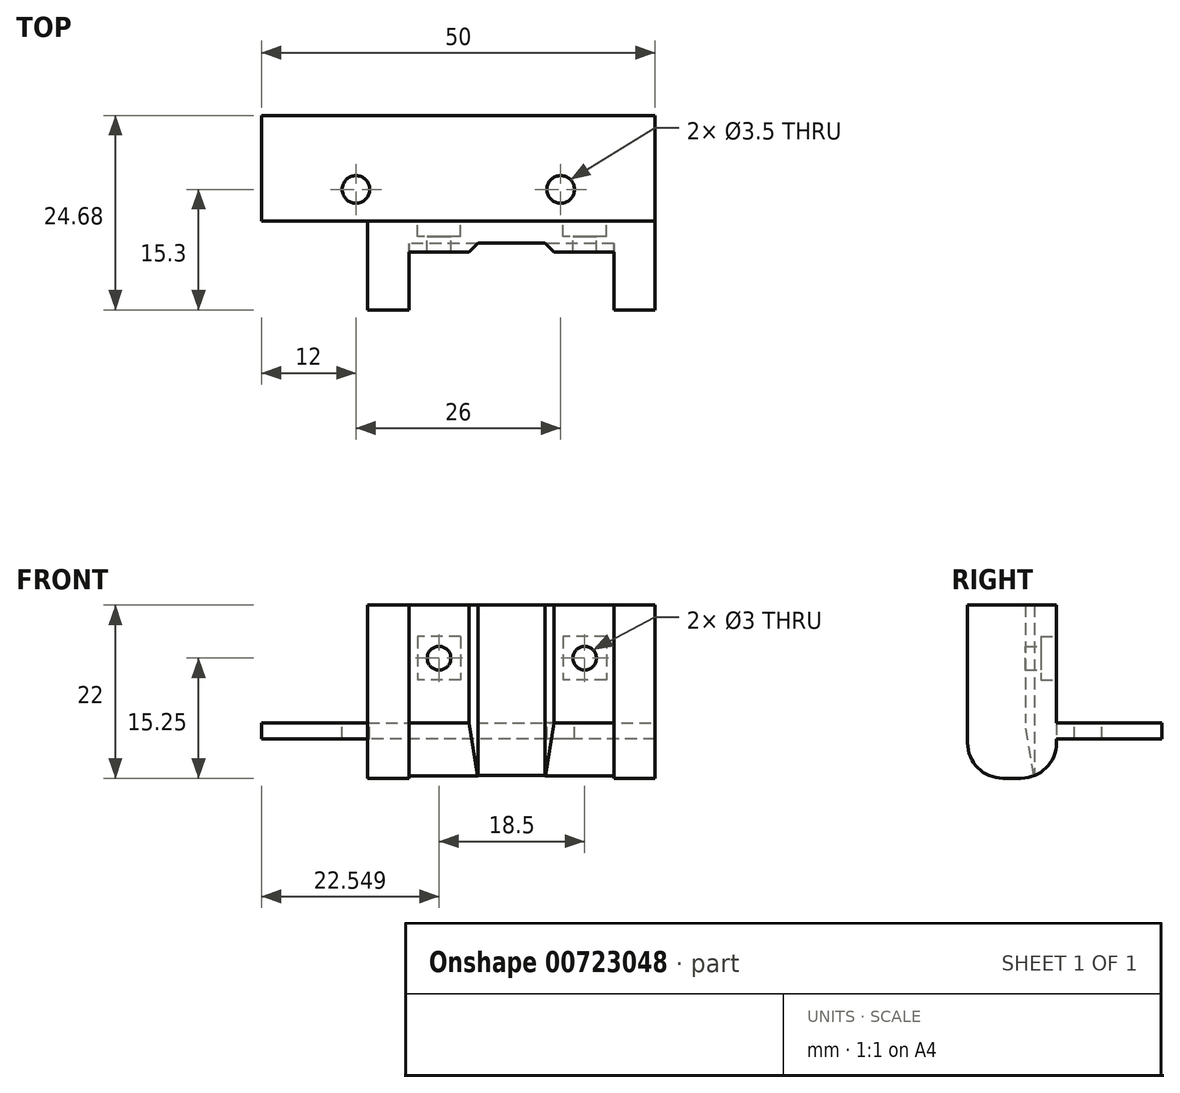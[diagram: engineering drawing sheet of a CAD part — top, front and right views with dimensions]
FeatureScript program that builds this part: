
annotation { "Feature Type Name" : "Feature", "Feature Type Description" : "" }
export const myFeature = defineFeature(function(context is Context, id is Id, definition is map)
    precondition{}
    {
        {
            var Q0;
            Q0=qCreatedBy(makeId("Right.planeOp"),FACE);
            var sketch = newSketch(context, id + "F0", { "sketchPlane" : qUnion([Q0])});
            skLineSegment(sketch, "E0", {"start": v(0, 0) * mm, "end": v(13.38, 0) * mm});
            skLineSegment(sketch, "E1", {"start": v(13.38, 0) * mm, "end": v(13.38, 2) * mm});
            skLineSegment(sketch, "E2", {"start": v(13.38, 2) * mm, "end": v(0, 2) * mm});
            skLineSegment(sketch, "E3", {"start": v(0, 2) * mm, "end": v(0, 0) * mm});
            skSolve(sketch);
        }
        {
            var Q0;
            Q0=makeQuery(id+"F0.imprint","IMPRINT",FACE,{"disambiguationData":[TD([[makeQuery(id+"F0.imprint","IMPRINT",EDGE,{"derivedFrom":sQuery(id+"F0.wireOp",EDGE,"E0")}),1.0]])]});
            extrude(context, id + "F1", {"entities" : qUnion([Q0]), "endBound" : BoundingType.SYMMETRIC, "depth" : 50 * mm});
        }
        {
            var Q0;
            Q0=makeQuery(id+"F1.opExtrude","SWEPT_FACE",FACE,{"disambiguationData":[OSD([sQuery(id+"F0.wireOp",EDGE,"E2")])]});
            var sketch = newSketch(context, id + "F2", { "sketchPlane" : qUnion([Q0])});
            skLineSegment(sketch, "E4", {"start": v(-25, 4) * mm, "end": v(25, 4) * mm, "construction": true});
            skLineSegment(sketch, "E5", {"start": v(0, 13.38) * mm, "end": v(0, 0) * mm, "construction": true});
            skCircle(sketch, "E6", {"center": v(-13, 4) * mm, "radius": 1.75 * mm});
            skCircle(sketch, "E7", {"center": v(13, 4) * mm, "radius": 1.75 * mm});
            skSolve(sketch);
        }
        {
            var Q0;
            Q0=qSketchRegion(id+"F2",true);
            extrude(context, id + "F3", {"entities" : qUnion([Q0]), "operationType" : NewBodyOperationType.REMOVE, "endBound" : BoundingType.UP_TO_NEXT, "oppositeDirection" : true, "depth" : 25 * mm});
        }
        {
            var Q0;
            Q0=qCreatedBy(makeId("Right.planeOp"),FACE);
            var sketch = newSketch(context, id + "F4", { "sketchPlane" : qUnion([Q0])});
            skLineSegment(sketch, "E8.bottom", {"start": v(0, 2) * mm, "end": v(-11.3, 2) * mm});
            skLineSegment(sketch, "E8.top", {"start": v(0, -5) * mm, "end": v(-11.3, -5) * mm});
            skLineSegment(sketch, "E8.left", {"start": v(0, 2) * mm, "end": v(0, -5) * mm});
            skLineSegment(sketch, "E8.right", {"start": v(-11.3, 2) * mm, "end": v(-11.3, -5) * mm});
            skSolve(sketch);
        }
        {
            var Q0;
            Q0=qSketchRegion(id+"F4",true);
            var Q1;
            Q1=makeQuery(id+"F1.opExtrude","CAP_FACE",FACE,{"disambiguationData":[OSD([sQuery(id+"F0.wireOp",EDGE,"E0"),sQuery(id+"F0.wireOp",EDGE,"E1"),sQuery(id+"F0.wireOp",EDGE,"E2"),sQuery(id+"F0.wireOp",EDGE,"E3")])],"isStart":false});
            extrude(context, id + "F5", {"entities" : qUnion([Q0]), "operationType" : NewBodyOperationType.ADD, "endBound" : BoundingType.UP_TO_SURFACE, "endBoundEntityFace" : qUnion([Q1]), "depth" : 36.5 * mm, "hasSecondDirection" : true, "secondDirectionOppositeDirection" : true, "secondDirectionDepth" : 11.5 * mm});
        }
        {
            var Q0;
            Q0=makeQuery(id+"F5.opExtrude","SWEPT_FACE",FACE,{"disambiguationData":[OSD([sQuery(id+"F4.wireOp",EDGE,"E8.top")])]});
            var sketch = newSketch(context, id + "F6", { "sketchPlane" : qUnion([Q0])});
            skLineSegment(sketch, "E9.bottom", {"start": v(-6.25, 11.3) * mm, "end": v(19.75, 11.3) * mm});
            skLineSegment(sketch, "E9.top", {"start": v(-6.25, 4.8) * mm, "end": v(19.75, 4.8) * mm});
            skLineSegment(sketch, "E9.left", {"start": v(-6.25, 11.3) * mm, "end": v(-6.25, 4.8) * mm});
            skLineSegment(sketch, "E9.right", {"start": v(19.75, 11.3) * mm, "end": v(19.75, 4.8) * mm});
            skLineSegment(sketch, "E10", {"start": v(6.75, 11.3) * mm, "end": v(6.75, 0) * mm, "construction": true});
            skSolve(sketch);
        }
        {
            var Q0;
            Q0=qSketchRegion(id+"F6",true);
            extrude(context, id + "F7", {"entities" : qUnion([Q0]), "operationType" : NewBodyOperationType.REMOVE, "endBound" : BoundingType.UP_TO_NEXT, "oppositeDirection" : true, "depth" : 25 * mm});
        }
        {
            var Q0;
            Q0=makeQuery(id+"F5.opExtrude","SWEPT_FACE",FACE,{"disambiguationData":[OSD([sQuery(id+"F4.wireOp",EDGE,"E8.top")])]});
            var sketch = newSketch(context, id + "F8", { "sketchPlane" : qUnion([Q0])});
            skLineSegment(sketch, "E11", {"start": v(6.75, 4.8) * mm, "end": v(6.75, 0) * mm, "construction": true});
            skLineSegment(sketch, "E12", {"start": v(0.5, 4.8) * mm, "end": v(2.5, 2.8) * mm});
            skLineSegment(sketch, "E13", {"start": v(2.5, 2.8) * mm, "end": v(11, 2.8) * mm});
            skLineSegment(sketch, "E14", {"start": v(11, 2.8) * mm, "end": v(13, 4.8) * mm});
            skLineSegment(sketch, "E15", {"start": v(13, 4.8) * mm, "end": v(0.5, 4.8) * mm});
            skSolve(sketch);
        }
        {
            var Q0;
            Q0=qSketchRegion(id+"F8",true);
            extrude(context, id + "F9", {"entities" : qUnion([Q0]), "operationType" : NewBodyOperationType.REMOVE, "endBound" : BoundingType.UP_TO_NEXT, "oppositeDirection" : true, "depth" : 25 * mm});
        }
        {
            var Q0;
            Q0=qCreatedBy(makeId("Right.planeOp"),FACE);
            var sketch = newSketch(context, id + "F10", { "sketchPlane" : qUnion([Q0])});
            skLineSegment(sketch, "E16", {"start": v(-2.8, -5) * mm, "end": v(-4.8, 7) * mm});
            skLineSegment(sketch, "E17", {"start": v(-4.8, 7) * mm, "end": v(-4.8, -5) * mm});
            skLineSegment(sketch, "E18", {"start": v(-4.8, -5) * mm, "end": v(-2.8, -5) * mm});
            skSolve(sketch);
        }
        {
            var Q0;
            Q0=qSketchRegion(id+"F10",true);
            var Q1;
            Q1=makeQuery(id+"F7.boolean.opBoolean","COPY",FACE,{"derivedFrom":makeQuery(id+"F7.opExtrude","SWEPT_FACE",FACE,{"disambiguationData":[OSD([sQuery(id+"F6.wireOp",EDGE,"E9.right")])]})});
            var Q2;
            Q2=makeQuery(id+"F7.boolean.opBoolean","COPY",FACE,{"derivedFrom":makeQuery(id+"F7.opExtrude","SWEPT_FACE",FACE,{"disambiguationData":[OSD([sQuery(id+"F6.wireOp",EDGE,"E9.left")])]})});
            extrude(context, id + "F11", {"entities" : qUnion([Q0]), "operationType" : NewBodyOperationType.REMOVE, "endBound" : BoundingType.UP_TO_SURFACE, "endBoundEntityFace" : qUnion([Q1]), "depth" : 25 * mm, "hasSecondDirection" : true, "secondDirectionBound" : SecondDirectionBoundingType.UP_TO_SURFACE, "secondDirectionOppositeDirection" : true, "secondDirectionBoundEntityFace" : qUnion([Q2]), "secondDirectionDepth" : 25 * mm});
        }
        {
            var Q0;
            {var subQ0=sQuery(id+"F4.wireOp",EDGE,"E8.right");var subQ1=sQuery(id+"F4.wireOp",EDGE,"E8.top");Q0=makeQuery(id+"F7.boolean.opBoolean","SPLIT",EDGE,{"disambiguationData":[TD([makeQuery(id+"F7.opExtrude","SWEPT_FACE",FACE,{"disambiguationData":[OSD([sQuery(id+"F6.wireOp",EDGE,"E9.left")])]})])],"derivedFrom":makeQuery(id+"F5.opExtrude","SWEPT_EDGE",EDGE,{"disambiguationData":[OSD([subQ1,subQ0])]})});}
            var Q1;
            {var subQ0=sQuery(id+"F4.wireOp",EDGE,"E8.right");var subQ1=sQuery(id+"F4.wireOp",EDGE,"E8.top");Q1=makeQuery(id+"F7.boolean.opBoolean","SPLIT",EDGE,{"disambiguationData":[TD([makeQuery(id+"F7.opExtrude","SWEPT_FACE",FACE,{"disambiguationData":[OSD([sQuery(id+"F6.wireOp",EDGE,"E9.right")])]})])],"derivedFrom":makeQuery(id+"F5.opExtrude","SWEPT_EDGE",EDGE,{"disambiguationData":[OSD([subQ1,subQ0])]})});}
            var Q2;
            Q2=makeQuery(id+"F5.opExtrude","SWEPT_EDGE",EDGE,{"disambiguationData":[OSD([sQuery(id+"F4.wireOp",EDGE,"E8.top"),sQuery(id+"F4.wireOp",EDGE,"E8.left")])]});
            fillet(context, id + "F12", {"entities" : qUnion([Q0, Q1, Q2]), "radius" : 4.5 * mm, "tangentPropagation" : true, "allowEdgeOverflow" : false});
        }
        {
            var Q0;
            Q0=makeQuery(id+"F5.boolean.opBoolean","MERGE",FACE,{"derivedFrom":[makeQuery(id+"F1.opExtrude","SWEPT_FACE",FACE,{"disambiguationData":[OSD([sQuery(id+"F0.wireOp",EDGE,"E2")])]}),makeQuery(id+"F5.opExtrude","SWEPT_FACE",FACE,{"disambiguationData":[OSD([sQuery(id+"F4.wireOp",EDGE,"E8.bottom")])]})]});
            var sketch = newSketch(context, id + "F13", { "sketchPlane" : qUnion([Q0])});
            skLineSegment(sketch, "E19", {"start": v(-11.5, 0) * mm, "end": v(25, 0) * mm});
            skSolve(sketch);
        }
        {
            var Q0;
            {var subQ23=sQuery(id+"F13.wireOp",EDGE,"E19");Q0=makeQuery(id+"F13.imprint","IMPRINT",FACE,{"disambiguationData":[TD([[makeQuery(id+"F13.imprint","IMPRINT",EDGE,{"derivedFrom":subQ23}),-1.0]])]});}
            extrude(context, id + "F14", {"entities" : qUnion([Q0]), "operationType" : NewBodyOperationType.ADD, "depth" : 15 * mm, "offsetDistance" : 25 * mm});
        }
        {
            var Q0;
            Q0=makeQuery(id+"F14.opExtrude","SWEPT_FACE",FACE,{"disambiguationData":[OSD([sQuery(id+"F13.wireOp",EDGE,"E19")])]});
            var sketch = newSketch(context, id + "F15", { "sketchPlane" : qUnion([Q0])});
            skLineSegment(sketch, "E20.bottom", {"start": v(-18.8, 13) * mm, "end": v(-13.3, 13) * mm});
            skLineSegment(sketch, "E20.top", {"start": v(-18.8, 7.5) * mm, "end": v(-13.3, 7.5) * mm});
            skLineSegment(sketch, "E20.left", {"start": v(-18.8, 13) * mm, "end": v(-18.8, 7.5) * mm});
            skLineSegment(sketch, "E20.right", {"start": v(-13.3, 13) * mm, "end": v(-13.3, 7.5) * mm});
            skPoint(sketch, "E20.middle", {"position": v(-16.05, 10.25) * mm});
            skLineSegment(sketch, "E21.bottom", {"start": v(-0.3, 13) * mm, "end": v(5.2, 13) * mm});
            skLineSegment(sketch, "E21.top", {"start": v(-0.3, 7.5) * mm, "end": v(5.2, 7.5) * mm});
            skLineSegment(sketch, "E21.left", {"start": v(-0.3, 13) * mm, "end": v(-0.3, 7.5) * mm});
            skLineSegment(sketch, "E21.right", {"start": v(5.2, 13) * mm, "end": v(5.2, 7.5) * mm});
            skPoint(sketch, "E21.middle", {"position": v(2.45, 10.25) * mm});
            skSolve(sketch);
        }
        {
            var Q0;
            {var subQ0=sQuery(id+"F15.wireOp",EDGE,"E20.bottom");Q0=makeQuery(id+"F15.imprint","IMPRINT",FACE,{"disambiguationData":[TD([[makeQuery(id+"F15.imprint","IMPRINT",EDGE,{"derivedFrom":subQ0}),-1.0]])]});}
            var Q1;
            {var subQ0=sQuery(id+"F15.wireOp",EDGE,"E21.bottom");Q1=makeQuery(id+"F15.imprint","IMPRINT",FACE,{"disambiguationData":[TD([[makeQuery(id+"F15.imprint","IMPRINT",EDGE,{"derivedFrom":subQ0}),-1.0]])]});}
            extrude(context, id + "F16", {"entities" : qUnion([Q0, Q1]), "operationType" : NewBodyOperationType.ADD, "oppositeDirection" : true, "depth" : 2 * mm, "offsetDistance" : 25 * mm});
        }
        {
            var Q0;
            {var subQ0=sQuery(id+"F15.wireOp",EDGE,"E20.bottom");Q0=makeQuery(id+"F15.imprint","IMPRINT",FACE,{"disambiguationData":[TD([[makeQuery(id+"F15.imprint","IMPRINT",EDGE,{"derivedFrom":subQ0}),-1.0]])]});}
            var Q1;
            {var subQ0=sQuery(id+"F15.wireOp",EDGE,"E21.bottom");Q1=makeQuery(id+"F15.imprint","IMPRINT",FACE,{"disambiguationData":[TD([[makeQuery(id+"F15.imprint","IMPRINT",EDGE,{"derivedFrom":subQ0}),-1.0]])]});}
            extrude(context, id + "F17", {"entities" : qUnion([Q0, Q1]), "operationType" : NewBodyOperationType.REMOVE, "oppositeDirection" : true, "depth" : 2 * mm, "offsetDistance" : 25 * mm});
        }
        {
            var Q0;
            Q0=sQuery(id+"F15.wireOp",VERTEX,"E21.middle");
            var Q1;
            Q1=sQuery(id+"F15.wireOp",VERTEX,"E20.middle");
            var Q2;
            Q2=makeQuery(id+"F1.opExtrude","SWEPT_BODY",BODY,{"disambiguationData":[OSD([sQuery(id+"F0.wireOp",EDGE,"E0"),sQuery(id+"F0.wireOp",EDGE,"E1"),sQuery(id+"F0.wireOp",EDGE,"E2"),sQuery(id+"F0.wireOp",EDGE,"E3")])]});
            hole(context, id + "F18", {"style" : HoleStyle.SIMPLE, "endStyle" : HoleEndStyle.THROUGH, "holeDiameter" : 3 * mm, "majorDiameter" : 5 * mm, "isTappedThrough" : true, "tappedDepth" : 12 * mm, "tapClearance" : 3, "locations" : qUnion([Q0, Q1]), "scope" : qUnion([Q2])});
        }
    });
